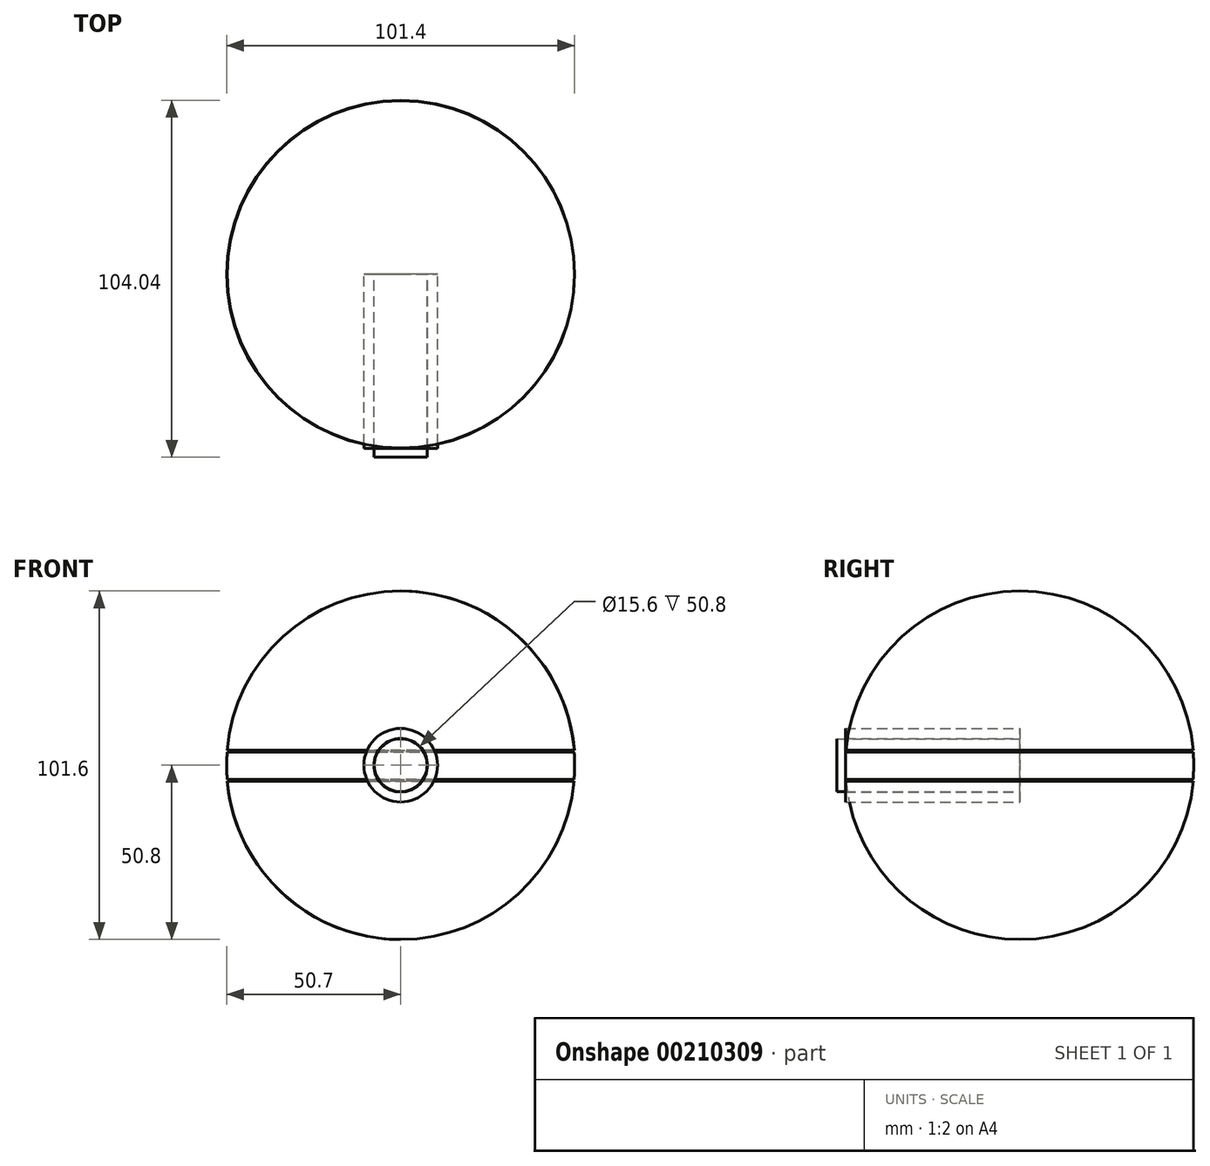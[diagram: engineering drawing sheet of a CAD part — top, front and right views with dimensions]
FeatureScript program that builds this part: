
annotation { "Feature Type Name" : "Feature", "Feature Type Description" : "" }
export const myFeature = defineFeature(function(context is Context, id is Id, definition is map)
    precondition{}
    {
        {
            var Q0;
            Q0=qCreatedBy(makeId("Front.planeOp"),FACE);
            var sketch = newSketch(context, id + "F0", { "sketchPlane" : qUnion([Q0])});
            skCircle(sketch, "E0", {"center": v(0, 0) * mm, "radius": 50.8 * mm});
            skLineSegment(sketch, "E1", {"start": v(0, 58.33) * mm, "end": v(0, -64.6) * mm});
            skLineSegment(sketch, "E2", {"start": v(61.04, 4.42) * mm, "end": v(-59.62, 4.42) * mm});
            skLineSegment(sketch, "E3", {"start": v(-59.62, -4.7) * mm, "end": v(61.04, -4.7) * mm});
            skSolve(sketch);
        }
        {
            var Q0;
            {var subQ0=sQuery(id+"F0.wireOp",EDGE,"E1");var subQ1=sQuery(id+"F0.wireOp",EDGE,"E0");var subQ2=makeQuery(id+"F0.imprint","INTERSECT",VERTEX,{"disambiguationData":[OD(0.0)],"derivedFrom":[subQ1,subQ0]});Q0=makeQuery(id+"F0.imprint","IMPRINT",FACE,{"disambiguationData":[TD([[makeQuery(id+"F0.imprint","IMPRINT",EDGE,{"disambiguationData":[TD([[subQ2,1.0]])],"derivedFrom":subQ1}),1.0]])]});}
            var Q1;
            {var subQ0=sQuery(id+"F0.wireOp",EDGE,"E3");var subQ1=sQuery(id+"F0.wireOp",EDGE,"E0");var subQ2=makeQuery(id+"F0.imprint","INTERSECT",VERTEX,{"disambiguationData":[OD(0.0)],"derivedFrom":[subQ1,subQ0]});Q1=makeQuery(id+"F0.imprint","IMPRINT",FACE,{"disambiguationData":[TD([[makeQuery(id+"F0.imprint","IMPRINT",EDGE,{"disambiguationData":[TD([[subQ2,-1.0]])],"derivedFrom":subQ1}),1.0]])]});}
            var Q2;
            Q2=sQuery(id+"F0.wireOp",EDGE,"E1");
            revolve(context, id + "F1", {"entities" : qUnion([Q0, Q1]), "axis" : qUnion([Q2]), "revolveType" : RevolveType.FULL});
        }
        {
            var Q0;
            Q0=qCreatedBy(makeId("Front.planeOp"),FACE);
            var sketch = newSketch(context, id + "F2", { "sketchPlane" : qUnion([Q0])});
            skLineSegment(sketch, "E4", {"start": v(-60.19, 3.83) * mm, "end": v(62.75, 3.83) * mm});
            skLineSegment(sketch, "E5", {"start": v(61.04, -4.13) * mm, "end": v(-60.47, -4.13) * mm});
            skCircle(sketch, "E6", {"center": v(0, 0) * mm, "radius": 50.7 * mm});
            skLineSegment(sketch, "E7", {"start": v(0, 59.47) * mm, "end": v(0, -65.75) * mm});
            skSolve(sketch);
        }
        {
            var Q0;
            {var subQ0=sQuery(id+"F2.wireOp",EDGE,"E6");var subQ1=sQuery(id+"F2.wireOp",EDGE,"E4");var subQ2=makeQuery(id+"F2.imprint","INTERSECT",VERTEX,{"disambiguationData":[OD(0.0)],"derivedFrom":[subQ1,subQ0]});Q0=makeQuery(id+"F2.imprint","IMPRINT",FACE,{"disambiguationData":[TD([[makeQuery(id+"F2.imprint","IMPRINT",EDGE,{"disambiguationData":[TD([[subQ2,-1.0]])],"derivedFrom":subQ1}),-1.0]])]});}
            var Q1;
            Q1=sQuery(id+"F2.wireOp",EDGE,"E7");
            revolve(context, id + "F3", {"operationType" : NewBodyOperationType.ADD, "entities" : qUnion([Q0]), "axis" : qUnion([Q1]), "revolveType" : RevolveType.FULL});
        }
        {
            var Q0;
            Q0=qCreatedBy(makeId("Front.planeOp"),FACE);
            var sketch = newSketch(context, id + "F4", { "sketchPlane" : qUnion([Q0])});
            skCircle(sketch, "E8", {"center": v(0, 0) * mm, "radius": 10.71 * mm});
            skCircle(sketch, "E9", {"center": v(0, 0) * mm, "radius": 7.8 * mm});
            skSolve(sketch);
        }
        {
            var Q0;
            Q0=makeQuery(id+"F4.imprint","IMPRINT",FACE,{"disambiguationData":[TD([[makeQuery(id+"F4.imprint","IMPRINT",EDGE,{"derivedFrom":sQuery(id+"F4.wireOp",EDGE,"E8")}),1.0]])]});
            extrude(context, id + "F5", {"entities" : qUnion([Q0]), "depth" : 50.8 * mm});
        }
        {
            var Q0;
            Q0=qCreatedBy(makeId("Front.planeOp"),FACE);
            var sketch = newSketch(context, id + "F6", { "sketchPlane" : qUnion([Q0])});
            skCircle(sketch, "E10", {"center": v(0, 0) * mm, "radius": 10.28 * mm});
            skCircle(sketch, "E11", {"center": v(0, 0) * mm, "radius": 7.7 * mm});
            skSolve(sketch);
        }
        {
            var Q0;
            Q0=makeQuery(id+"F6.imprint","IMPRINT",FACE,{"disambiguationData":[TD([[makeQuery(id+"F6.imprint","IMPRINT",EDGE,{"derivedFrom":sQuery(id+"F6.wireOp",EDGE,"E11")}),1.0]])]});
            extrude(context, id + "F7", {"entities" : qUnion([Q0]), "depth" : 53.34 * mm});
        }
    });
